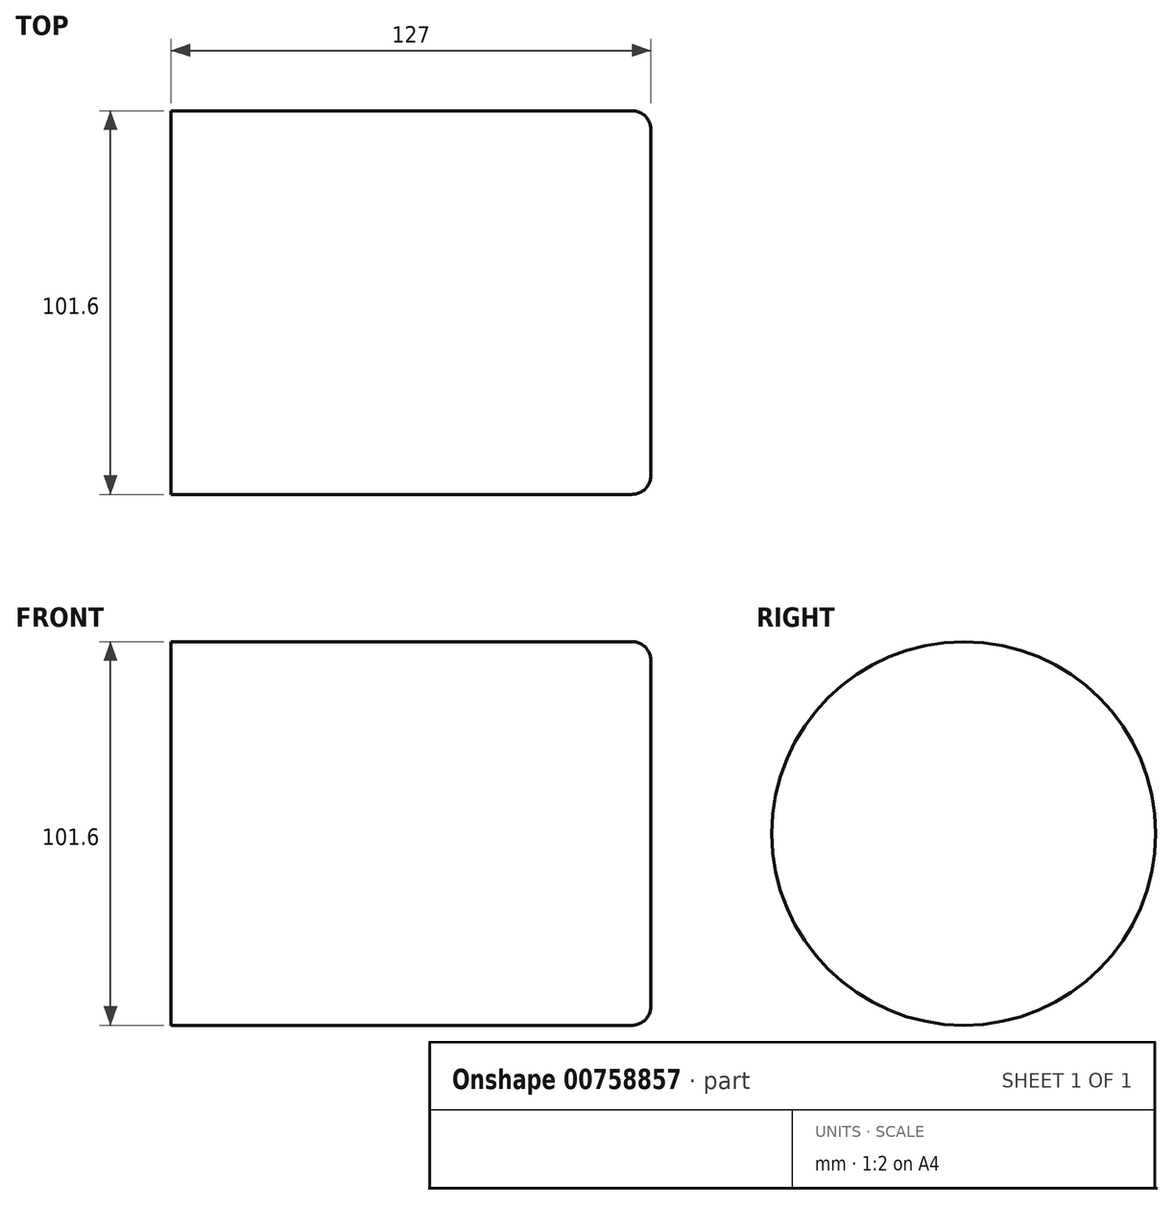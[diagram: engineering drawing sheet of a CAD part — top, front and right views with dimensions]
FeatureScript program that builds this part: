
annotation { "Feature Type Name" : "Feature", "Feature Type Description" : "" }
export const myFeature = defineFeature(function(context is Context, id is Id, definition is map)
    precondition{}
    {
        {
            var Q0;
            Q0=qCreatedBy(makeId("Front.planeOp"),FACE);
            var sketch = newSketch(context, id + "F0", { "sketchPlane" : qUnion([Q0])});
            skLineSegment(sketch, "E0", {"start": v(0, 0) * mm, "end": v(127, 0) * mm});
            skLineSegment(sketch, "E1", {"start": v(127, 0) * mm, "end": v(127, 50.8) * mm});
            skLineSegment(sketch, "E2", {"start": v(127, 50.8) * mm, "end": v(0, 50.8) * mm});
            skLineSegment(sketch, "E3", {"start": v(0, 50.8) * mm, "end": v(0, 0) * mm});
            skSolve(sketch);
        }
        {
            var Q0;
            Q0 = qSketchRegion(id + "F0", true);
            var Q1;
            Q1=sQuery(id+"F0.wireOp",EDGE,"E0");
            revolve(context, id + "F1", {"surfaceOperationType" : NewSurfaceOperationType.NEW, "entities" : qUnion([Q0]), "axis" : qUnion([Q1]), "revolveType" : RevolveType.FULL});
        }
        {
            var Q0;
            Q0=makeQuery(id+"F1.opRevolve","SWEPT_EDGE",EDGE,{"disambiguationData":[OSD([sQuery(id+"F0.wireOp",EDGE,"E1"),sQuery(id+"F0.wireOp",EDGE,"E2")])]});
            fillet(context, id + "F2", {"entities" : qUnion([Q0]), "radius" : 5.08 * mm, "tangentPropagation" : true, "allowEdgeOverflow" : false});
        }
    });
